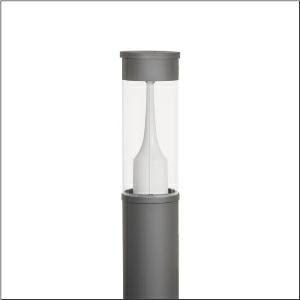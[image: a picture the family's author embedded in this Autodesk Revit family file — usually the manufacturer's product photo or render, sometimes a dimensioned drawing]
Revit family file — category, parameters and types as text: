
# Revit family: city-light_260_iq___p1_0a_5xa5295lf14h_3d8e
name_source: partatom
category: Lighting Fixtures
units: mm (PartAtom-declared; Revit-internal decimal feet)

## family parameters
Cut with Voids When Loaded = No
Host = Face
Light Source = No
Part Type = Normal
Room Calculation Point = No
Round Connector Dimension = Use Diameter
Shared = No

## types (1)
- --- (1 x LED, 1510 lm, 10 W, 4000K)
    Apparent Load = 10 VA
    CIE Flux Codes = 32 61 90 93 100
    Color Rendering = 70
    Color Temperature = 4000K
    Default Elevation = 1800 mm
    Description = City-Light 260 iQ, light pillar, Module 540 iQ-SR, primary light control with 3 zone facetted reflector, of plastic, silver coated, highly specular, structured, primary optical cover: cover, of PMMA, transparent, partly coated, light distribution: P1.0a, primary light characteristic: strongly asymmetric, LED, High Power LED, rated luminous flux: 1.510lm, luminous efficacy: 151lm/W, light colour: 740, colour temperature: 4000K, control gear: ECG iQ, control: presetting dimming logarithmic, Street-Remote, Auto-Match, Temp-Guard, Lumen-Switch, Night-Set, Smart-Wire, Light-Fading, Desk-Remote (wireless, voltage-free reading and setting of iQ features in the workshop via application-optimized NFC function/RFID function), optimised constant luminous flux control (CLO 2.0), with terminal, 6-pole, max. 2.5mm², mains connection: 230..240V, AC, 50/60Hz, start of lifetime: 10W, end of service life: 10W, reduction: 5W, luminaire housing, cylindrical, of extruded aluminium section, coated, Siteco® metallic grey (DB 702S), length: 2.600mm, diameter: 200mm, Module 540 iQ-SR, traffic white (RAL 9016), equipment: standard, protection rating (complete): IP65, insulation class (complete): insulation class II (safety insulation), certification: CE, ENEC, VDE, packaging unit: 1 piece

Light Distribution: P1.0a
    Height = 500 mm
    Lamp = 1 x LED
    Lamp Light Flux = 1510 lm
    Lamp Power = 10 W
    Lamp count = 1
    Length = 200 mm  [stored 0.656168 ft]
    Luminous efficacy = 151 lm/W
    Manufacturer = Siteco
    ModVariant = No
    Model = 5XA5295LF14H
    Mounting Place = Floor
    Mounting Type = Freestanding
    Number of Poles = 1
    OnlyDefault = Yes
    Power Factor = 1
    Product Name = City-Light 260 iQ | P1.0a
    Product group = light pillar
    ProductGroupID = 1303
    Protection Class = Protection class II
    Protection Degree = IP 65
    RLX_Detail_Level = 1
    RLX_Emergency_Light_Flux = 0 lm
    RLX_Emergency_Type = 0
    RLX_Emergency_Type_DB = No
    RlxData = <blob elided: 56941 chars, md5=8372288d>
    Socket = socket
    Standby Power = 0 W
    System Light Flux = 1510 lm
    System Power = 10 W
    Type Comments = factory setting: luminous flux: 100 % | dim-lin: 254 | 401 mA
    Type Image = l_1006918.jpg
    URL = http://relux.com
    VarID = @adj_109641
    Voltage = 0 V
    Weight = 0.00 kg
    Width = 0 mm  [stored 0 ft]

note: [stored X ft] marks values corroborated as IEEE doubles in the binary element streams (Revit-internal decimal feet)

## geometry (parser evidence)
native form markers: Blend x4, Sweep x12
no freeform markers — native parametric forms only
